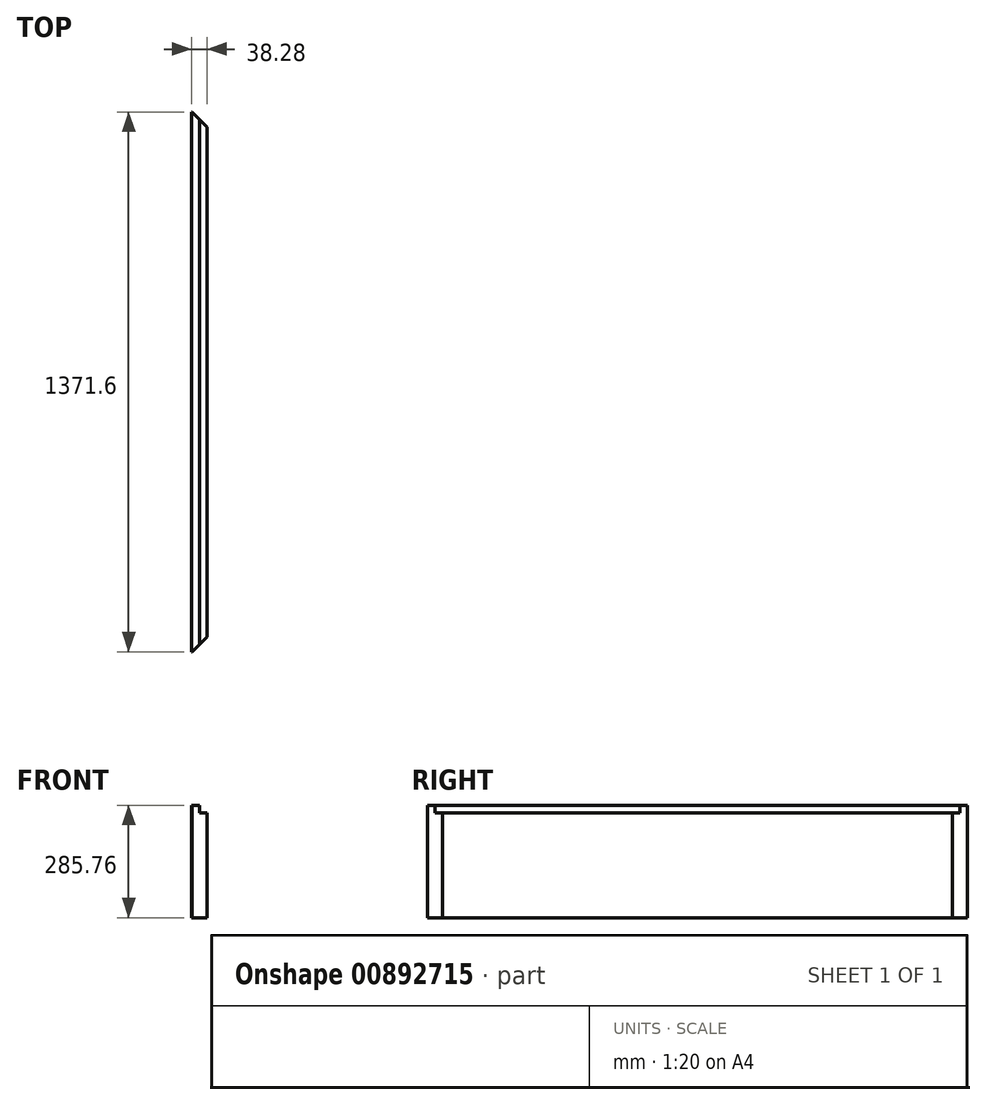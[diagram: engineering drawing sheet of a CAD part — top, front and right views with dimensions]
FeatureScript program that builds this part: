
annotation { "Feature Type Name" : "Feature", "Feature Type Description" : "" }
export const myFeature = defineFeature(function(context is Context, id is Id, definition is map)
    precondition{}
    {
        {
            var Q0;
            Q0=qCreatedBy(makeId("Front.planeOp"),FACE);
            var sketch = newSketch(context, id + "F0", { "sketchPlane" : qUnion([Q0])});
            skLineSegment(sketch, "E0.bottom", {"start": v(19.14, 142.87) * mm, "end": v(-19.14, 142.87) * mm});
            skLineSegment(sketch, "E0.top", {"start": v(19.14, -142.88) * mm, "end": v(-19.14, -142.88) * mm});
            skLineSegment(sketch, "E0.left", {"start": v(19.14, 142.87) * mm, "end": v(19.14, -142.88) * mm});
            skLineSegment(sketch, "E0.right", {"start": v(-19.14, 142.87) * mm, "end": v(-19.14, -142.88) * mm});
            skPoint(sketch, "E0.middle", {"position": v(0, 0) * mm});
            skSolve(sketch);
        }
        {
            var Q0;
            Q0=qSketchRegion(id+"F0",true);
            extrude(context, id + "F1", {"entities" : qUnion([Q0]), "depth" : 1371.6 * mm, "offsetDistance" : 25.4 * mm});
        }
        {
            var Q0;
            Q0=makeQuery(id+"F1.opExtrude","CAP_EDGE",EDGE,{"disambiguationData":[OSD([sQuery(id+"F0.wireOp",EDGE,"E0.left")])],"isStart":false});
            var Q1;
            Q1=makeQuery(id+"F1.opExtrude","CAP_EDGE",EDGE,{"disambiguationData":[OSD([sQuery(id+"F0.wireOp",EDGE,"E0.left")])],"isStart":true});
            chamfer(context, id + "F2", {"entities" : qUnion([Q0, Q1]), "width" : 38.1 * mm, "tangentPropagation" : true});
        }
        {
            var Q0;
            Q0=makeQuery(id+"F1.opExtrude","SWEPT_FACE",FACE,{"disambiguationData":[OSD([sQuery(id+"F0.wireOp",EDGE,"E0.left")])]});
            var sketch = newSketch(context, id + "F3", { "sketchPlane" : qUnion([Q0])});
            skLineSegment(sketch, "E1.bottom", {"start": v(-1352.55, 142.87) * mm, "end": v(-19.05, 142.87) * mm});
            skLineSegment(sketch, "E1.top", {"start": v(-1352.55, 123.83) * mm, "end": v(-19.05, 123.83) * mm});
            skLineSegment(sketch, "E1.left", {"start": v(-1352.55, 142.87) * mm, "end": v(-1352.55, 123.83) * mm});
            skLineSegment(sketch, "E1.right", {"start": v(-19.05, 142.87) * mm, "end": v(-19.05, 123.83) * mm});
            skSolve(sketch);
        }
        {
            var Q0;
            Q0 = qSketchRegion(id + "F3", true);
            extrude(context, id + "F4", {"entities" : qUnion([Q0]), "operationType" : NewBodyOperationType.REMOVE, "oppositeDirection" : true, "depth" : 19.05 * mm, "offsetDistance" : 25.4 * mm});
        }
    });
